# Revit family: Air-Curtain_Climate-Control_PoweredAire_TGD
name_source: partatom
category: Mechanical Equipment
revit_build: Autodesk Revit 2018 (Build: 20170927_1515(x64)
units: mm (PartAtom-declared; Revit-internal decimal feet)

## family parameters
Cut with Voids When Loaded = No
Host = Face
OmniClass Number = 23.75.35.17.21
OmniClass Title = Air Curtains
Part Type = Normal
Room Calculation Point = No
Round Connector Dimension = Use Diameter
Shared = No

## types (7) — shared parameters
Assembly Code = D3090400
Construction Details = http://www.arcat.com
Default Elevation = 0' - 0"
Exhaust Connection Diameter = 0' - 5"
Green Building-LEED = http://www.arcat.com
HVAC_BTU Input = 0.0 Btu/h
HVAC_Primary CFM = 0 CFM
HVAC_Temperature Rise = 105 °F
Heating Element Load = 0 W
Keynote = 23 34 33
Manufacturer = Powered Aire, Inc
Manufacturer Fax = 724-588-3371
Manufacturer Website = http://www.poweredaire.com
Max Height = 12' - 0"
Motor HP = 0.75
Motor RPM = 1630
Overall Depth = 5' - 4 1/4"
Power Rating = 0 W
Product Data = http://www.arcat.com
Revision = R1_2016-08
Sales Information = http://www.poweredaire.com
Sound Pressure = >63 dBA
Specification = http://www.arcat.com
Standards Conformance = Made in USA
URL = http://www.poweredaire.com
Unit Depth = 2' - 3 1/4"
Unit Height = 1' - 9"
Unit Width Notes = Other Widths available.
zero-valued in all types: Expected Lifespan (Years), Filter Weight, Maintenance Schedule (Months), Warranty Duration (Years)

## per-type parameters (varying)
| type | Description | HVAC_BTU Output | HVAC_Outlet Velocity | HVAC_Outlet Velocity Uniformity | HVAC_Outlet Volume | Intake Width | Model | Motor Count | Mounting Width | Nozzle Width | Unit Weight | Unit Width |
| 144'' Nozzle | Powered Aire Direct Gas Heated Climate Control Air Curtain - TDG-4-144 as Specified | 1153000.0 Btu/h | 3700 FPM | 0.95 | 10200 CFM | 10' - 0" | TDG-4-144 | 4 | 12' - 1 23/32" | 12' - 0 7/32" | 860 | 12' - 3 7/32" |
| 132'' Nozzle | Powered Aire Direct Gas Heated Climate Control Air Curtain - TDG-3-132 as Specified | 861000.0 Btu/h | 2800 FPM | 0.94 | 7600 CFM | 8' - 0" | TDG-3-132 | 3 | 11' - 1 21/32" | 11' - 0 5/32" | 780 | 11' - 3 5/32" |
| 120'' Nozzle | Powered Aire Direct Gas Heated Climate Control Air Curtain - TDG-3-120 as Specified | 864000.0 Btu/h | 3200 FPM | 0.95 | 7600 CFM | 8' - 0" | TDG-3-120 | 3 | 10' - 1 21/32" | 10' - 0 5/32" | 760 | 10' - 3 5/32" |
| 108'' Nozzle | Powered Aire Direct Gas Heated Climate Control Air Curtain - TDG-3-108 as Specified | 865000.0 Btu/h | 3700 FPM | 0.92 | 7600 CFM | 8' - 0" | TDG-3-108 | 3 | 9' - 1 21/32" | 9' - 0 5/32" | 660 | 9' - 3 5/32" |
| 96'' Nozzle | Powered Aire Direct Gas Heated Climate Control Air Curtain - TDG-2-96 as Specified | 576000.0 Btu/h | 2800 FPM | 0.92 | 5100 CFM | 6' - 1" | TDG-2-96 | 2 | 8' - 1 9/16" | 8' - 0 1/16" | 600 | 8' - 3 1/16" |
| 84'' Nozzle | Powered Aire Direct Gas Heated Climate Control Air Curtain - TDG-2-84 as Specified | 574000.0 Btu/h | 3200 FPM | 0.93 | 5100 CFM | 6' - 1" | TDG-2-84 | 2 | 7' - 1 9/16" | 7' - 0 1/16" | 550 | 7' - 3 1/16" |
| 72'' Nozzle | Powered Aire Direct Gas Heated Climate Control Air Curtain - TDG-2-72 as Specified | 576000.0 Btu/h | 3700 FPM | 0.95 | 5100 CFM | 6' - 1" | TDG-2-72 | 2 | 6' - 1 9/16" | 6' - 0 1/16" | 500 | 6' - 3 1/16" |

## geometry (parser evidence)
native form markers: Sweep x1
no freeform markers — native parametric forms only
